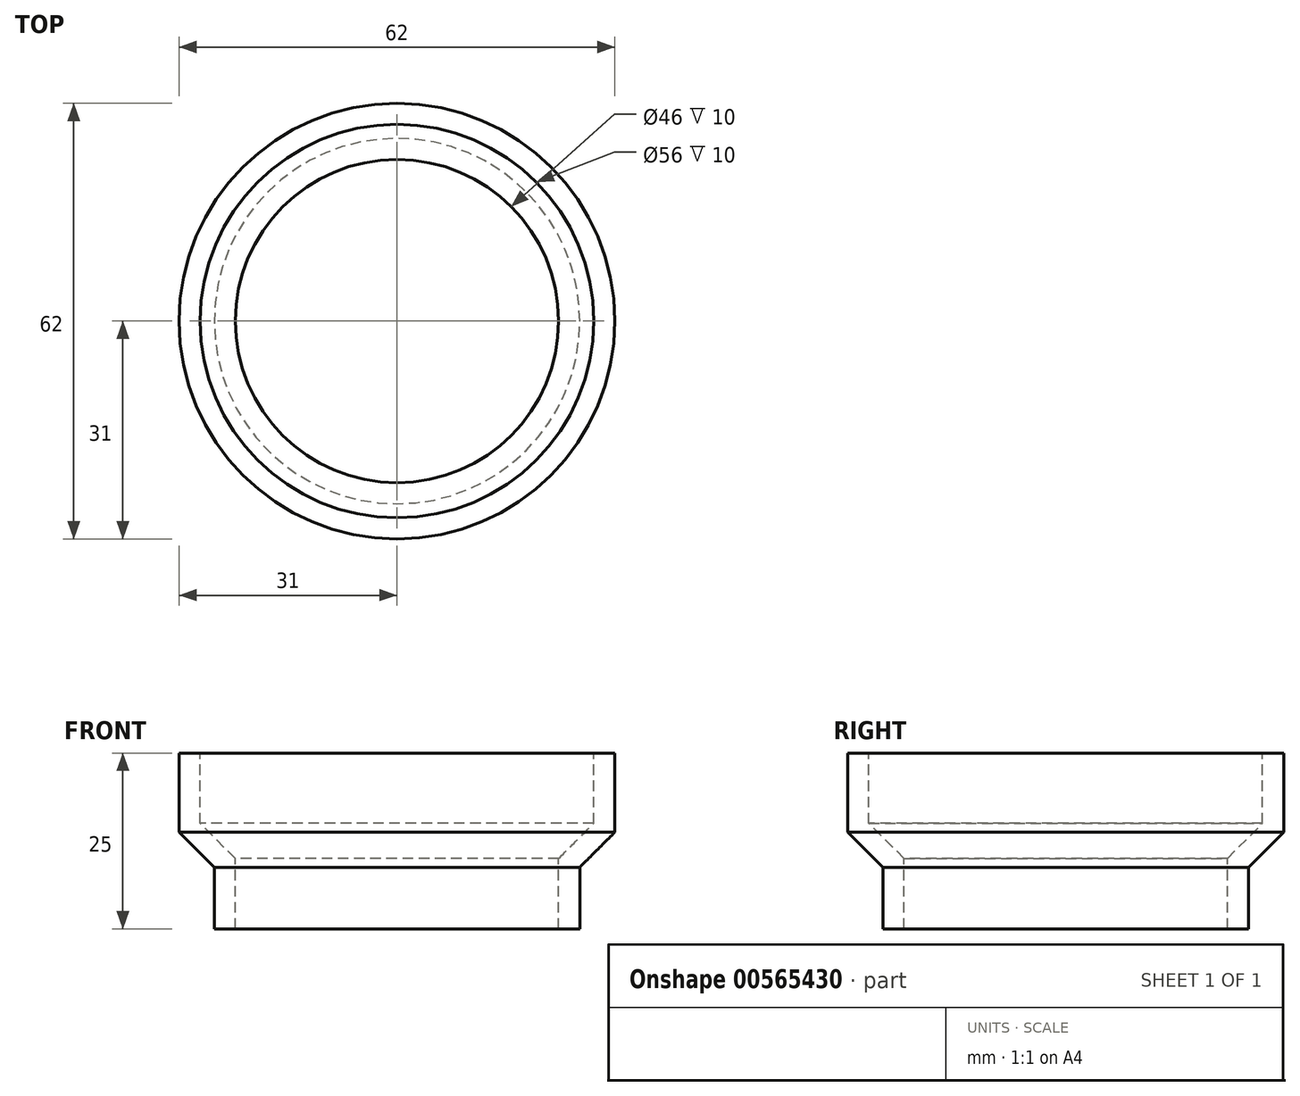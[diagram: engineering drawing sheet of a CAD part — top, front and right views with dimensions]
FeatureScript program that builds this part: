
annotation { "Feature Type Name" : "Feature", "Feature Type Description" : "" }
export const myFeature = defineFeature(function(context is Context, id is Id, definition is map)
    precondition{}
    {
        {
            var Q0;
            Q0=qCreatedBy(makeId("Front.planeOp"),FACE);
            var sketch = newSketch(context, id + "F0", { "sketchPlane" : qUnion([Q0])});
            skLineSegment(sketch, "E0", {"start": v(-28, 11.52) * mm, "end": v(-28, 1.52) * mm});
            skLineSegment(sketch, "E1", {"start": v(-23, -3.48) * mm, "end": v(-23, -13.48) * mm});
            skLineSegment(sketch, "E2", {"start": v(-23, -13.48) * mm, "end": v(-26, -13.48) * mm});
            skLineSegment(sketch, "E3", {"start": v(-26, -13.48) * mm, "end": v(-26, -4.72) * mm});
            skLineSegment(sketch, "E4", {"start": v(-26, -4.72) * mm, "end": v(-31, 0.28) * mm});
            skLineSegment(sketch, "E5", {"start": v(-31, 0.28) * mm, "end": v(-31, 11.52) * mm});
            skLineSegment(sketch, "E6", {"start": v(-31, 11.52) * mm, "end": v(-28, 11.52) * mm});
            skLineSegment(sketch, "E7", {"start": v(0, 2.08) * mm, "end": v(0, -1.06) * mm, "construction": true});
            skLineSegment(sketch, "E8", {"start": v(-28, 1.52) * mm, "end": v(-23, -3.48) * mm});
            skLineSegment(sketch, "E9", {"start": v(0, 6.52) * mm, "end": v(0, -8.48) * mm});
            skPoint(sketch, "E9.endSnap0", {"position": v(-23, -8.48) * mm});
            skSolve(sketch);
        }
        {
            var Q0;
            Q0=makeQuery(id+"F0.imprint","IMPRINT",FACE,{"disambiguationData":[TD([[makeQuery(id+"F0.imprint","IMPRINT",EDGE,{"derivedFrom":sQuery(id+"F0.wireOp",EDGE,"E0")}),-1.0]])]});
            var Q1;
            Q1=sQuery(id+"F0.wireOp",EDGE,"E7");
            revolve(context, id + "F1", {"entities" : qUnion([Q0]), "axis" : qUnion([Q1]), "revolveType" : RevolveType.FULL});
        }
    });
